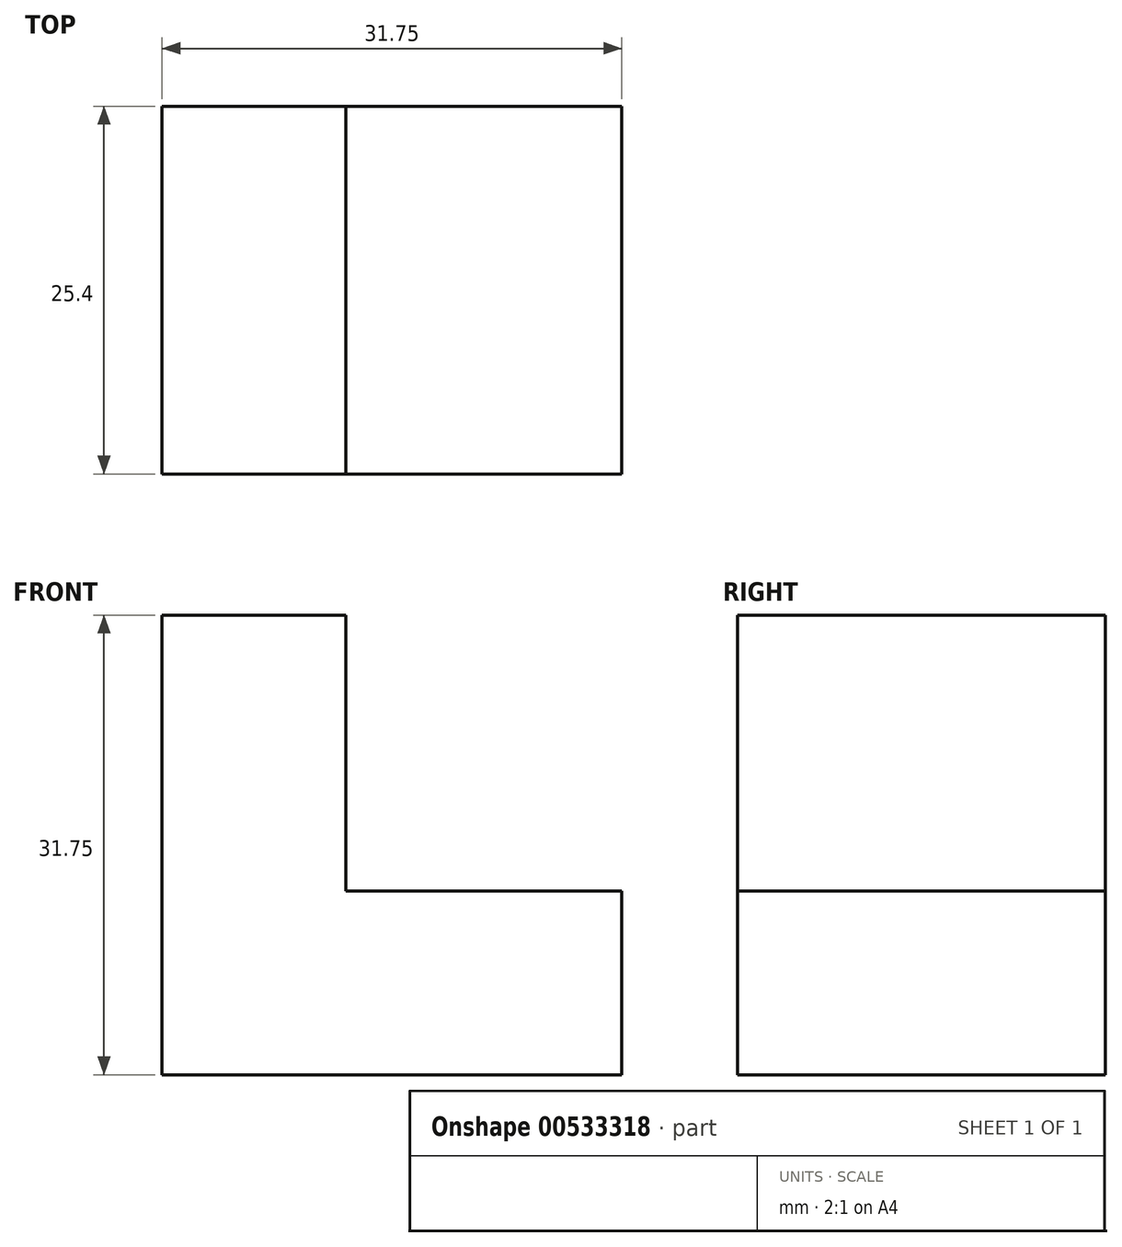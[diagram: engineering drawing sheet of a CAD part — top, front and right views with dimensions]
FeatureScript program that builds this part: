
annotation { "Feature Type Name" : "Feature", "Feature Type Description" : "" }
export const myFeature = defineFeature(function(context is Context, id is Id, definition is map)
    precondition{}
    {
        {
            var Q0;
            Q0=qCreatedBy(makeId("Front.planeOp"),FACE);
            var sketch = newSketch(context, id + "F0", { "sketchPlane" : qUnion([Q0])});
            skLineSegment(sketch, "E0", {"start": v(0, 0) * mm, "end": v(0, 31.75) * mm});
            skLineSegment(sketch, "E1", {"start": v(0, 31.75) * mm, "end": v(12.7, 31.75) * mm});
            skLineSegment(sketch, "E2", {"start": v(12.7, 31.75) * mm, "end": v(12.7, 12.7) * mm});
            skLineSegment(sketch, "E3", {"start": v(12.7, 12.7) * mm, "end": v(31.75, 12.7) * mm});
            skLineSegment(sketch, "E4", {"start": v(31.75, 12.7) * mm, "end": v(31.75, 0) * mm});
            skLineSegment(sketch, "E5", {"start": v(0, 0) * mm, "end": v(31.75, 0) * mm});
            skLineSegment(sketch, "E6", {"start": v(0, 0) * mm, "end": v(-6.23, 0) * mm});
            skSolve(sketch);
        }
        {
            var Q0;
            Q0=makeQuery(id+"F0.imprint","IMPRINT",FACE,{"disambiguationData":[TD([[makeQuery(id+"F0.imprint","IMPRINT",EDGE,{"derivedFrom":sQuery(id+"F0.wireOp",EDGE,"E0")}),-1.0]])]});
            extrude(context, id + "F1", {"entities" : qUnion([Q0]), "depth" : 25.4 * mm, "offsetDistance" : 25.4 * mm});
        }
    });
